# Revit family: QF_ELECTROLUXPROFESSIONAL_589586_MCJHEBK8AO
name_source: partatom
category: Specialty Equipment
revit_build: Autodesk Revit 2018 (Build: 20190510_1515(x64)
units: mm (PartAtom-declared; Revit-internal decimal feet)

## family parameters
Always vertical = Yes
Cut with Voids When Loaded = No
Part Type = Normal
Room Calculation Point = No
Round Connector Dimension = Use Diameter
Shared = No
Work Plane-Based = No

## types (1)
- QF_ELECTROLUXPROFESSIONAL_589586_MCJHEBK8AO
    Apparent Power = 33000 VA
    Cold Water Flow = 0 GPM
    Cold Water Maximum Pressure = 0.00 psi
    Cold Water Minimum Pressure = 0.00 psi
    Cold Water Size = 1"
    Description = FULL IND+S.OVEN,TAP(L)1S,BS,1200X900X700
    Direct Waste Size = 0"
    Electrical Remarks = 400 V/3N ph/50/60 Hz
    FL Amps = 48 A
    HP = 44.3 HP
    Hot Water Consumption = 0 GPM
    Hot Water Maximum Pressure = 0.00 psi
    Hot Water Minimum Pressure = 0.00 psi
    Hot Water Size = 1"
    Manufacturer = ELECTROLUX
    Max Overcurrent Protection = 0 A
    Min Ckt Ampacity = 0 A
    Model = 589586
    Phase = 3
    Volts = 400 V
    Watts = 33000 W
    Weight in Pounds = 487.22

## geometry (parser evidence)
native form markers: Blend x40, Sweep x16
no freeform markers — native parametric forms only
